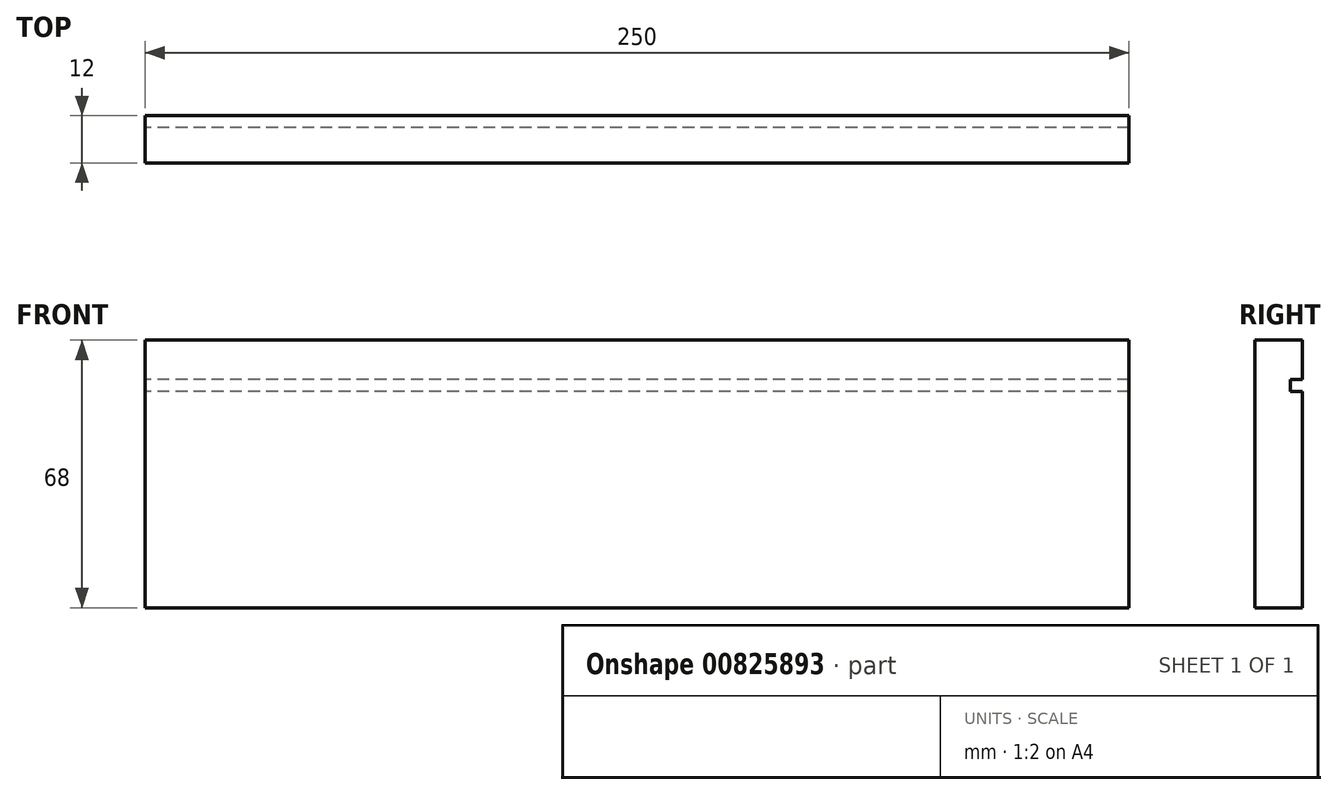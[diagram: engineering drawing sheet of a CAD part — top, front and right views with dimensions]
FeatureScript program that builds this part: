
annotation { "Feature Type Name" : "Feature", "Feature Type Description" : "" }
export const myFeature = defineFeature(function(context is Context, id is Id, definition is map)
    precondition{}
    {
        {
            var Q0;
            Q0=qCreatedBy(makeId("Right.planeOp"),FACE);
            var sketch = newSketch(context, id + "F0", { "sketchPlane" : qUnion([Q0])});
            skLineSegment(sketch, "E0.bottom", {"start": v(6, -34) * mm, "end": v(-6, -34) * mm});
            skLineSegment(sketch, "E0.top", {"start": v(6, 34) * mm, "end": v(-6, 34) * mm});
            skLineSegment(sketch, "E0.left", {"start": v(6, -34) * mm, "end": v(6, 34) * mm});
            skLineSegment(sketch, "E0.right", {"start": v(-6, -34) * mm, "end": v(-6, 34) * mm});
            skPoint(sketch, "E0.middle", {"position": v(0, 0) * mm});
            skLineSegment(sketch, "E1", {"start": v(6, 24) * mm, "end": v(3, 24) * mm});
            skLineSegment(sketch, "E2", {"start": v(3, 24) * mm, "end": v(3, 21) * mm});
            skLineSegment(sketch, "E3", {"start": v(3, 21) * mm, "end": v(6, 21) * mm});
            skSolve(sketch);
        }
        {
            var Q0;
            {var subQ3=sQuery(id+"F0.wireOp",EDGE,"E0.bottom");Q0=makeQuery(id+"F0.imprint","IMPRINT",FACE,{"disambiguationData":[TD([[makeQuery(id+"F0.imprint","IMPRINT",EDGE,{"derivedFrom":subQ3}),-1.0]])]});}
            extrude(context, id + "F1", {"entities" : qUnion([Q0]), "endBound" : BoundingType.SYMMETRIC, "depth" : 250 * mm, "offsetDistance" : 25.4 * mm});
        }
    });
